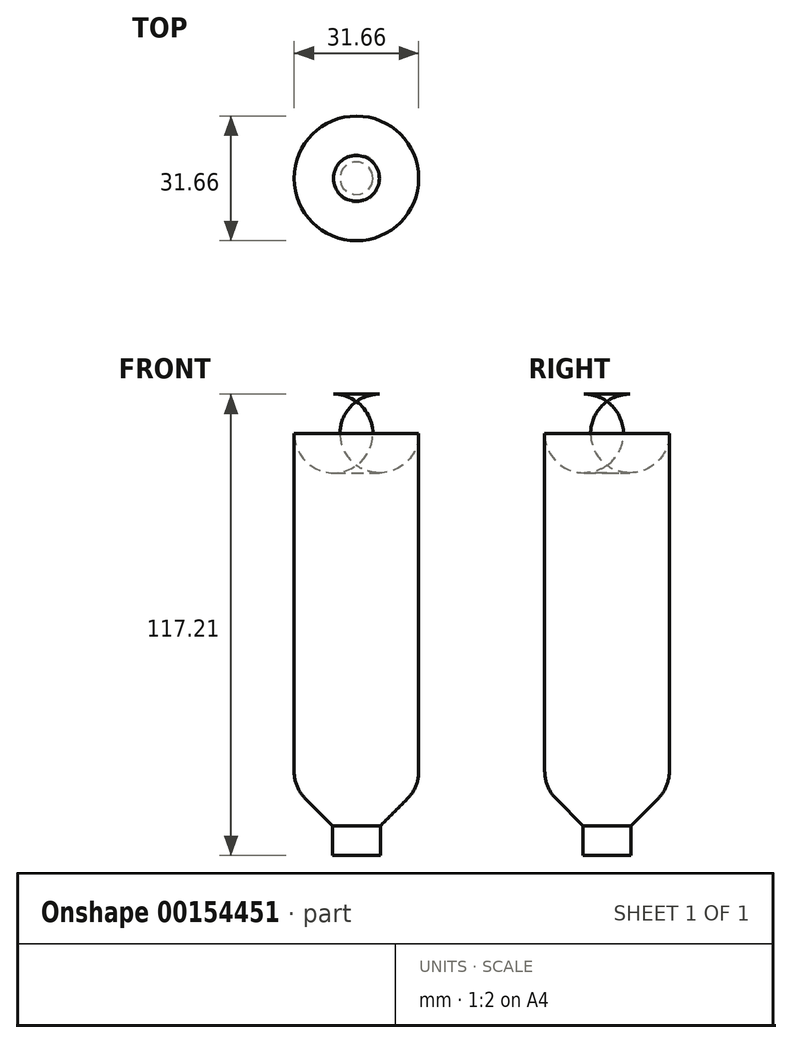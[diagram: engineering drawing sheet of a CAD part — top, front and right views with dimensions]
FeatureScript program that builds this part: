
annotation { "Feature Type Name" : "Feature", "Feature Type Description" : "" }
export const myFeature = defineFeature(function(context is Context, id is Id, definition is map)
    precondition{}
    {
        {
            var Q0;
            Q0=qCreatedBy(makeId("Front.planeOp"),FACE);
            var sketch = newSketch(context, id + "F0", { "sketchPlane" : qUnion([Q0])});
            skLineSegment(sketch, "E0.bottom", {"start": v(-15.83, 117.21) * mm, "end": v(0, 117.21) * mm});
            skLineSegment(sketch, "E0.left", {"start": v(-15.83, 117.21) * mm, "end": v(-15.83, 17.27) * mm});
            skLineSegment(sketch, "E0.right", {"start": v(0, 117.21) * mm, "end": v(0, 0) * mm});
            skLineSegment(sketch, "E1.top", {"start": v(-6.09, 0) * mm, "end": v(0, 0) * mm});
            skLineSegment(sketch, "E1.left", {"start": v(-6.09, 7.53) * mm, "end": v(-6.09, 0) * mm});
            skPoint(sketch, "E2.newPointA", {"position": v(0, 0) * mm});
            skLineSegment(sketch, "E3", {"start": v(-15.83, 17.27) * mm, "end": v(-6.09, 7.53) * mm});
            skSolve(sketch);
        }
        {
            var Q0;
            Q0=makeQuery(id+"F0.imprint","IMPRINT",FACE,{"disambiguationData":[TD([[makeQuery(id+"F0.imprint","IMPRINT",EDGE,{"derivedFrom":sQuery(id+"F0.wireOp",EDGE,"E0.bottom")}),-1.0]])]});
            var Q1;
            Q1=sQuery(id+"F0.wireOp",EDGE,"E0.right");
            revolve(context, id + "F1", {"entities" : qUnion([Q0]), "axis" : qUnion([Q1]), "revolveType" : RevolveType.FULL});
        }
        {
            var Q0;
            Q0=makeQuery(id+"F1.opRevolve","SWEPT_EDGE",EDGE,{"disambiguationData":[OSD([sQuery(id+"F0.wireOp",EDGE,"E0.bottom"),sQuery(id+"F0.wireOp",EDGE,"E0.left")])]});
            var Q1;
            Q1=makeQuery(id+"F1.opRevolve","SWEPT_EDGE",EDGE,{"disambiguationData":[OSD([sQuery(id+"F0.wireOp",EDGE,"E0.left"),sQuery(id+"F0.wireOp",EDGE,"E3")])]});
            fillet(context, id + "F2", {"entities" : qUnion([Q0, Q1]), "radius" : 10 * mm, "tangentPropagation" : true, "allowEdgeOverflow" : false});
        }
    });
